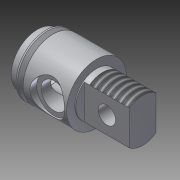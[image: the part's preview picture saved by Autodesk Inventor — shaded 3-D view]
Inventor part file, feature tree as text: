
AUTODESK INVENTOR PART (.ipt)
format: ipt  version: 2014 SP1 (Build 180222100, 222)  size: 187,392 bytes
history: native  units: in
note: dims shown in document units (in); Inventor stores cm internally (conversion verified against a paired STEP export)
features: extrude x4, sketch x3, thread x2, revolve x1, plane x1
ambient origin geometry x8: Origin, YZ Plane, XZ Plane, XY Plane, X Axis, Y Axis, Z Axis, Center Point
bodies: Solid1 (feature_tree)
feature tree (11):
  sketch  "Sketch1"  dims[d1=0.86in d2=0.375in]
  revolve  "Revolution1"  [1 undecoded]
  extrude  "Extrusion2"  Depth=0.25in
  plane  "Work Plane1"
  extrude  "Extrusion3"  Depth=0.125in
  extrude  "Extrusion4"  Depth=0.625in
  extrude  "Extrusion5"  Depth=0.015in
  thread  "Thread1"  [1 undecoded]
  thread  "Thread2"  [1 undecoded]
  sketch  "Sketch2"  dims[d4=0.09in d5=0.25in]
  sketch  "Sketch3"  dims[d6=0.34in d8=0.624in d9=0.625in d10=0.015in d11=45.0deg d12=0.62in d13=0.7in d14=0.75in d15=0.625in d17=0.38in d18=0.625in d19=0.38in d20=90.0deg d26=1.0in d27=0.0in d28=0.5in d29=0.1875in d30=0.1in d31=0.0in d32=0.38in d33=0.65in d34=0.0in d35=0.625in d36=0.0in d37=0.125in d38=0.325in d39=1.0in d40=0.0in d41=1.0in d42=0.0in]
note: 3 required parameter values undecoded (feature->parameter linkage not recoverable at this tier; creation-order binding heuristic only, values carry confidence <= 0.55)